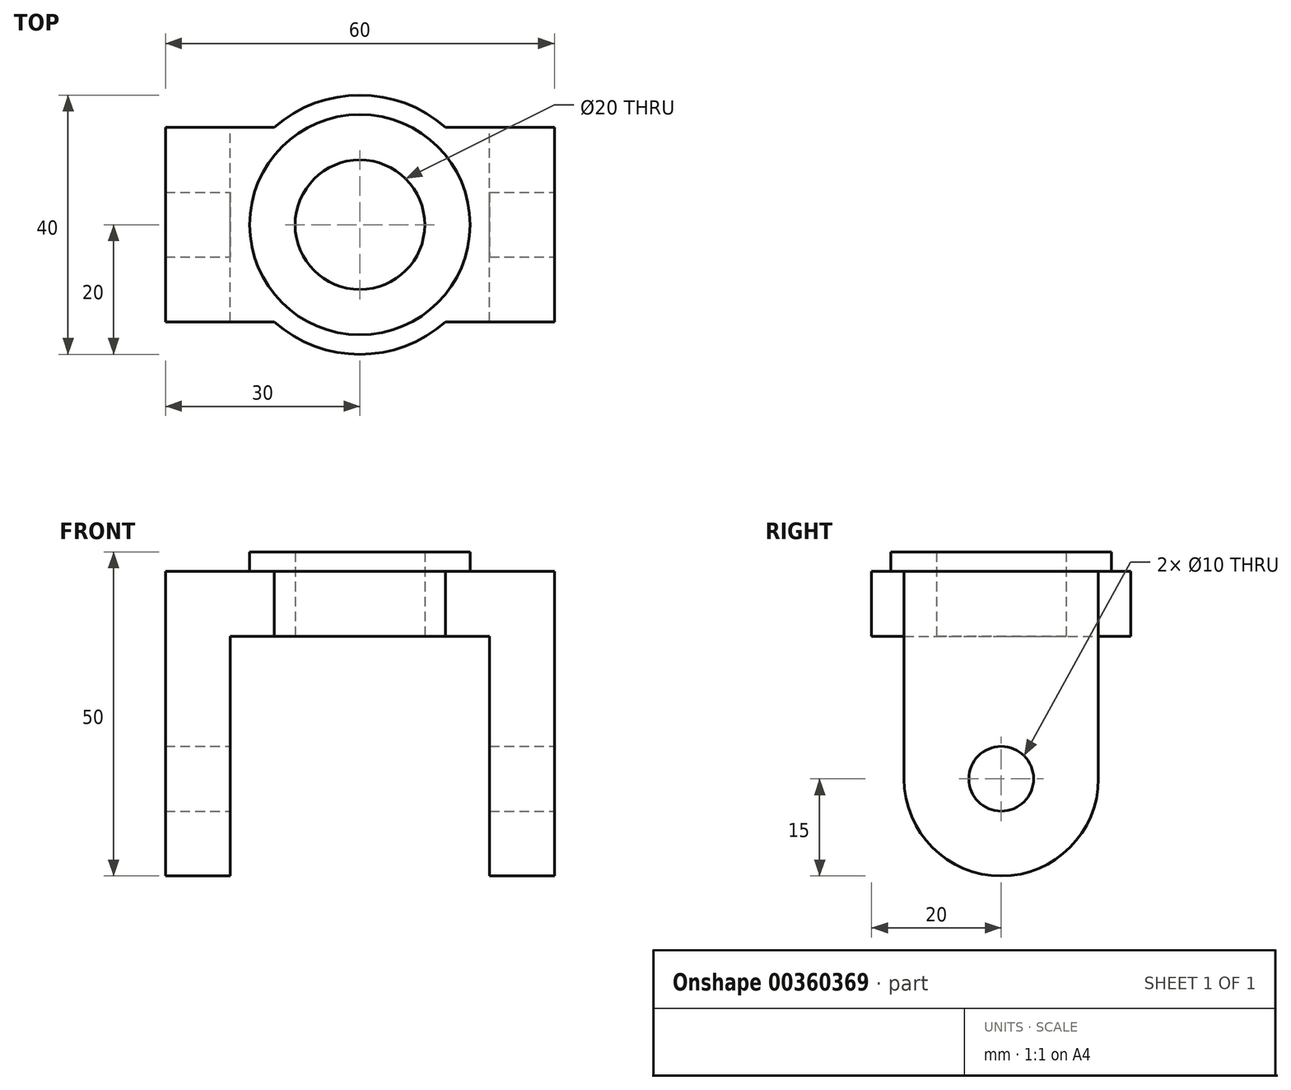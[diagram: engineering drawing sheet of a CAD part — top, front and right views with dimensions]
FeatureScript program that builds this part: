
annotation { "Feature Type Name" : "Feature", "Feature Type Description" : "" }
export const myFeature = defineFeature(function(context is Context, id is Id, definition is map)
    precondition{}
    {
        {
            var Q0;
            Q0=qCreatedBy(makeId("Top.planeOp"),FACE);
            var sketch = newSketch(context, id + "F0", { "sketchPlane" : qUnion([Q0])});
            skLineSegment(sketch, "E0.bottom", {"start": v(30, 15) * mm, "end": v(-30, 15) * mm});
            skLineSegment(sketch, "E0.top", {"start": v(30, -15) * mm, "end": v(-30, -15) * mm});
            skLineSegment(sketch, "E0.left", {"start": v(30, 15) * mm, "end": v(30, -15) * mm});
            skLineSegment(sketch, "E0.right", {"start": v(-30, 15) * mm, "end": v(-30, -15) * mm});
            skPoint(sketch, "E0.middle", {"position": v(0, 0) * mm});
            skCircle(sketch, "E1", {"center": v(0, 0) * mm, "radius": 20 * mm});
            skCircle(sketch, "E2", {"center": v(0, 0) * mm, "radius": 10 * mm});
            skSolve(sketch);
        }
        {
            var Q0;
            Q0 = qSketchRegion(id + "F0", true);
            extrude(context, id + "F1", {"entities" : qUnion([Q0]), "depth" : 10 * mm});
        }
        {
            var Q0;
            Q0=makeQuery(id+"F1.opExtrude","CAP_FACE",FACE,{"disambiguationData":[OSD([sQuery(id+"F0.wireOp",EDGE,"E0.bottom"),sQuery(id+"F0.wireOp",EDGE,"E0.top"),sQuery(id+"F0.wireOp",EDGE,"E0.left"),sQuery(id+"F0.wireOp",EDGE,"E0.right"),sQuery(id+"F0.wireOp",EDGE,"E1"),sQuery(id+"F0.wireOp",EDGE,"E2")])],"isStart":false});
            var sketch = newSketch(context, id + "F2", { "sketchPlane" : qUnion([Q0])});
            skCircle(sketch, "E3", {"center": v(0, 0) * mm, "radius": 17 * mm});
            skSolve(sketch);
        }
        {
            var Q0;
            Q0=makeQuery(id+"F2.imprint","IMPRINT",FACE,{"disambiguationData":[TD([[makeQuery(id+"F2.imprint","IMPRINT",EDGE,{"derivedFrom":sQuery(id+"F2.wireOp",EDGE,"E3")}),1.0]])]});
            extrude(context, id + "F3", {"entities" : qUnion([Q0]), "operationType" : NewBodyOperationType.ADD, "depth" : 3 * mm});
        }
        {
            var Q0;
            Q0=makeQuery(id+"F1.opExtrude","CAP_FACE",FACE,{"disambiguationData":[OSD([sQuery(id+"F0.wireOp",EDGE,"E0.bottom"),sQuery(id+"F0.wireOp",EDGE,"E0.top"),sQuery(id+"F0.wireOp",EDGE,"E0.left"),sQuery(id+"F0.wireOp",EDGE,"E0.right"),sQuery(id+"F0.wireOp",EDGE,"E1"),sQuery(id+"F0.wireOp",EDGE,"E2")])],"isStart":true});
            var sketch = newSketch(context, id + "F4", { "sketchPlane" : qUnion([Q0])});
            skLineSegment(sketch, "E4.bottom", {"start": v(-30, 15) * mm, "end": v(-20, 15) * mm});
            skLineSegment(sketch, "E4.top", {"start": v(-30, -15) * mm, "end": v(-20, -15) * mm});
            skLineSegment(sketch, "E4.left", {"start": v(-30, 15) * mm, "end": v(-30, -15) * mm});
            skLineSegment(sketch, "E4.right", {"start": v(-20, 15) * mm, "end": v(-20, -15) * mm});
            skLineSegment(sketch, "E5.bottom", {"start": v(20, 15) * mm, "end": v(30, 15) * mm});
            skLineSegment(sketch, "E5.top", {"start": v(20, -15) * mm, "end": v(30, -15) * mm});
            skLineSegment(sketch, "E5.left", {"start": v(20, 15) * mm, "end": v(20, -15) * mm});
            skLineSegment(sketch, "E5.right", {"start": v(30, 15) * mm, "end": v(30, -15) * mm});
            skSolve(sketch);
        }
        {
            var Q0;
            Q0=makeQuery(id+"F4.imprint","IMPRINT",FACE,{"disambiguationData":[TD([[makeQuery(id+"F4.imprint","IMPRINT",EDGE,{"derivedFrom":sQuery(id+"F4.wireOp",EDGE,"E4.bottom")}),1.0]])]});
            var Q1;
            Q1=makeQuery(id+"F4.imprint","IMPRINT",FACE,{"disambiguationData":[TD([[makeQuery(id+"F4.imprint","IMPRINT",EDGE,{"derivedFrom":sQuery(id+"F4.wireOp",EDGE,"E5.bottom")}),1.0]])]});
            extrude(context, id + "F5", {"entities" : qUnion([Q0, Q1]), "operationType" : NewBodyOperationType.ADD, "depth" : 37 * mm});
        }
        {
            var Q0;
            Q0=makeQuery(id+"F5.boolean.opBoolean","MERGE",FACE,{"derivedFrom":[makeQuery(id+"F1.opExtrude","SWEPT_FACE",FACE,{"disambiguationData":[OSD([sQuery(id+"F0.wireOp",EDGE,"E0.left")])]}),makeQuery(id+"F5.opExtrude","SWEPT_FACE",FACE,{"disambiguationData":[OSD([sQuery(id+"F4.wireOp",EDGE,"E5.right")])]})]});
            var sketch = newSketch(context, id + "F6", { "sketchPlane" : qUnion([Q0])});
            skPoint(sketch, "E6", {"position": v(0, -22) * mm});
            skCircle(sketch, "E7", {"center": v(0, -22) * mm, "radius": 15 * mm});
            skCircle(sketch, "E8", {"center": v(0, -22) * mm, "radius": 5 * mm});
            skSolve(sketch);
        }
        {
            var Q0;
            {var subQ0=sQuery(id+"F6.wireOp",EDGE,"E7");var subQ1=sQuery(id+"F4.wireOp",EDGE,"E5.right");var subQ4=makeQuery(id+"F5.opExtrude","CAP_EDGE",EDGE,{"disambiguationData":[OSD([subQ1])],"isStart":false});var subQ5=makeQuery(id+"F6.imprint","INTERSECT",VERTEX,{"derivedFrom":[subQ4,subQ0]});Q0=makeQuery(id+"F6.imprint","IMPRINT",FACE,{"disambiguationData":[TD([[makeQuery(id+"F6.imprint","IMPRINT",EDGE,{"disambiguationData":[TD([[subQ5,1.0]])],"derivedFrom":subQ0}),-1.0]])]});}
            var Q1;
            {var subQ0=sQuery(id+"F6.wireOp",EDGE,"E7");var subQ1=sQuery(id+"F4.wireOp",EDGE,"E5.right");var subQ4=makeQuery(id+"F5.opExtrude","CAP_EDGE",EDGE,{"disambiguationData":[OSD([subQ1])],"isStart":false});var subQ5=makeQuery(id+"F6.imprint","INTERSECT",VERTEX,{"derivedFrom":[subQ4,subQ0]});Q1=makeQuery(id+"F6.imprint","IMPRINT",FACE,{"disambiguationData":[TD([[makeQuery(id+"F6.imprint","IMPRINT",EDGE,{"disambiguationData":[TD([[subQ5,-1.0]])],"derivedFrom":subQ0}),-1.0]])]});}
            var Q2;
            Q2=makeQuery(id+"F6.imprint","IMPRINT",FACE,{"disambiguationData":[TD([[makeQuery(id+"F6.imprint","IMPRINT",EDGE,{"derivedFrom":sQuery(id+"F6.wireOp",EDGE,"E8")}),1.0]])]});
            extrude(context, id + "F7", {"entities" : qUnion([Q0, Q1, Q2]), "operationType" : NewBodyOperationType.REMOVE, "endBound" : BoundingType.THROUGH_ALL, "oppositeDirection" : true, "depth" : 25 * mm});
        }
    });
